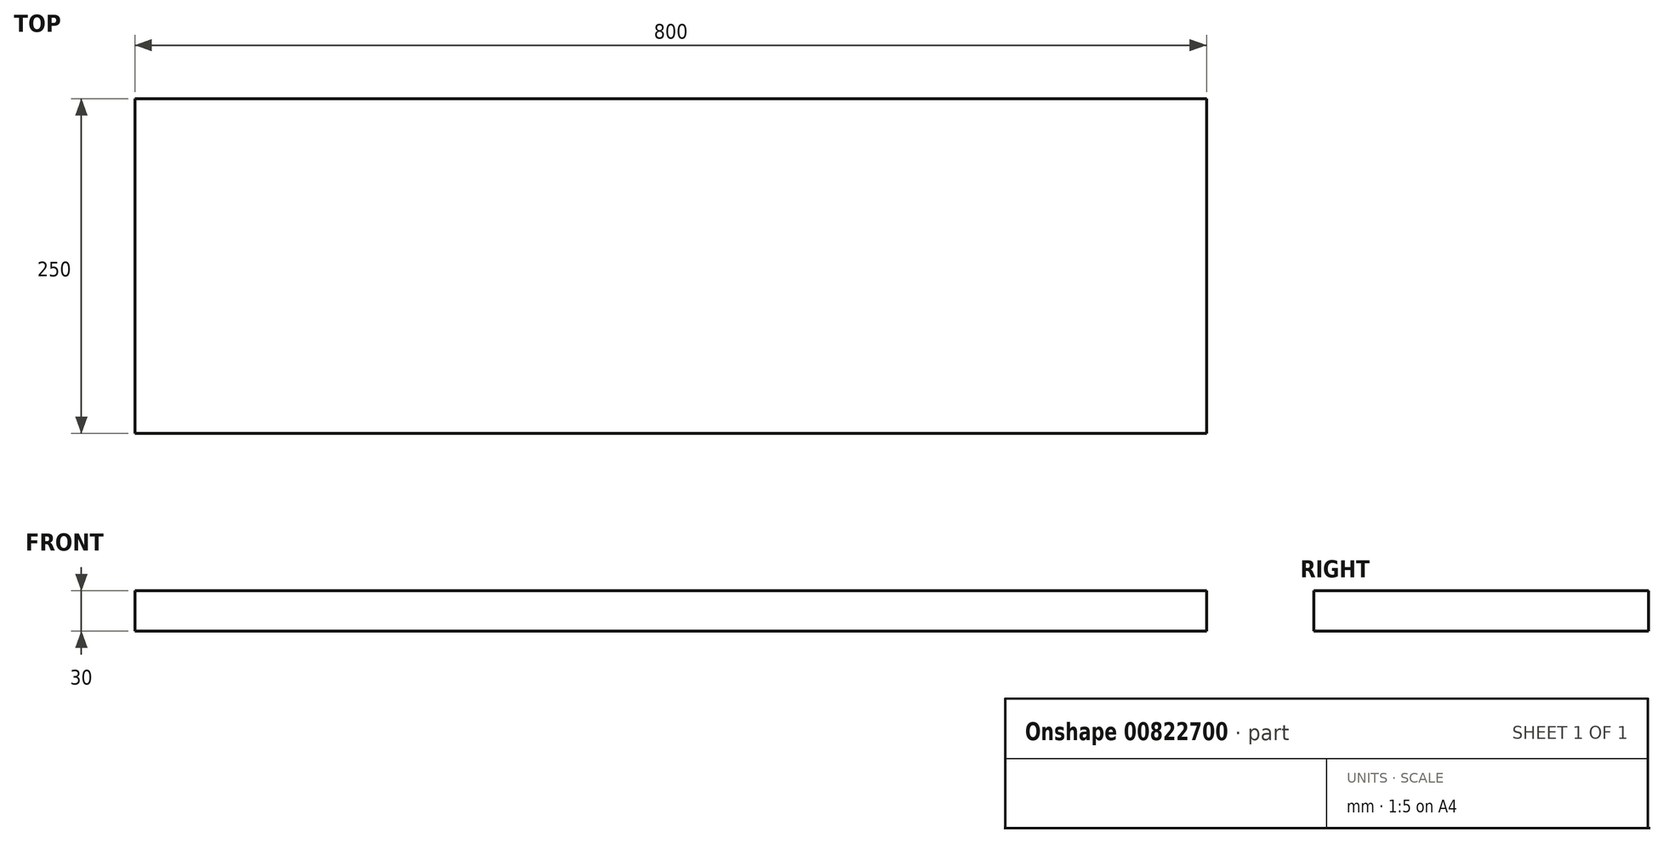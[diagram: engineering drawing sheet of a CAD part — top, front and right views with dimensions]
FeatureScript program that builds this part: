
annotation { "Feature Type Name" : "Feature", "Feature Type Description" : "" }
export const myFeature = defineFeature(function(context is Context, id is Id, definition is map)
    precondition{}
    {
        {
            var Q0;
            Q0=qCreatedBy(makeId("Top.planeOp"),FACE);
            var sketch = newSketch(context, id + "F0", { "sketchPlane" : qUnion([Q0])});
            skLineSegment(sketch, "E0.bottom", {"start": v(0, 0) * mm, "end": v(800, 0) * mm});
            skLineSegment(sketch, "E0.top", {"start": v(0, 250) * mm, "end": v(800, 250) * mm});
            skLineSegment(sketch, "E0.left", {"start": v(0, 0) * mm, "end": v(0, 250) * mm});
            skLineSegment(sketch, "E0.right", {"start": v(800, 0) * mm, "end": v(800, 250) * mm});
            skSolve(sketch);
        }
        {
            var Q0;
            Q0=makeQuery(id+"F0.imprint","IMPRINT",FACE,{"disambiguationData":[TD([[makeQuery(id+"F0.imprint","IMPRINT",EDGE,{"derivedFrom":sQuery(id+"F0.wireOp",EDGE,"E0.bottom")}),1.0]])]});
            extrude(context, id + "F1", {"entities" : qUnion([Q0]), "depth" : 30 * mm, "offsetDistance" : 25 * mm});
        }
    });
